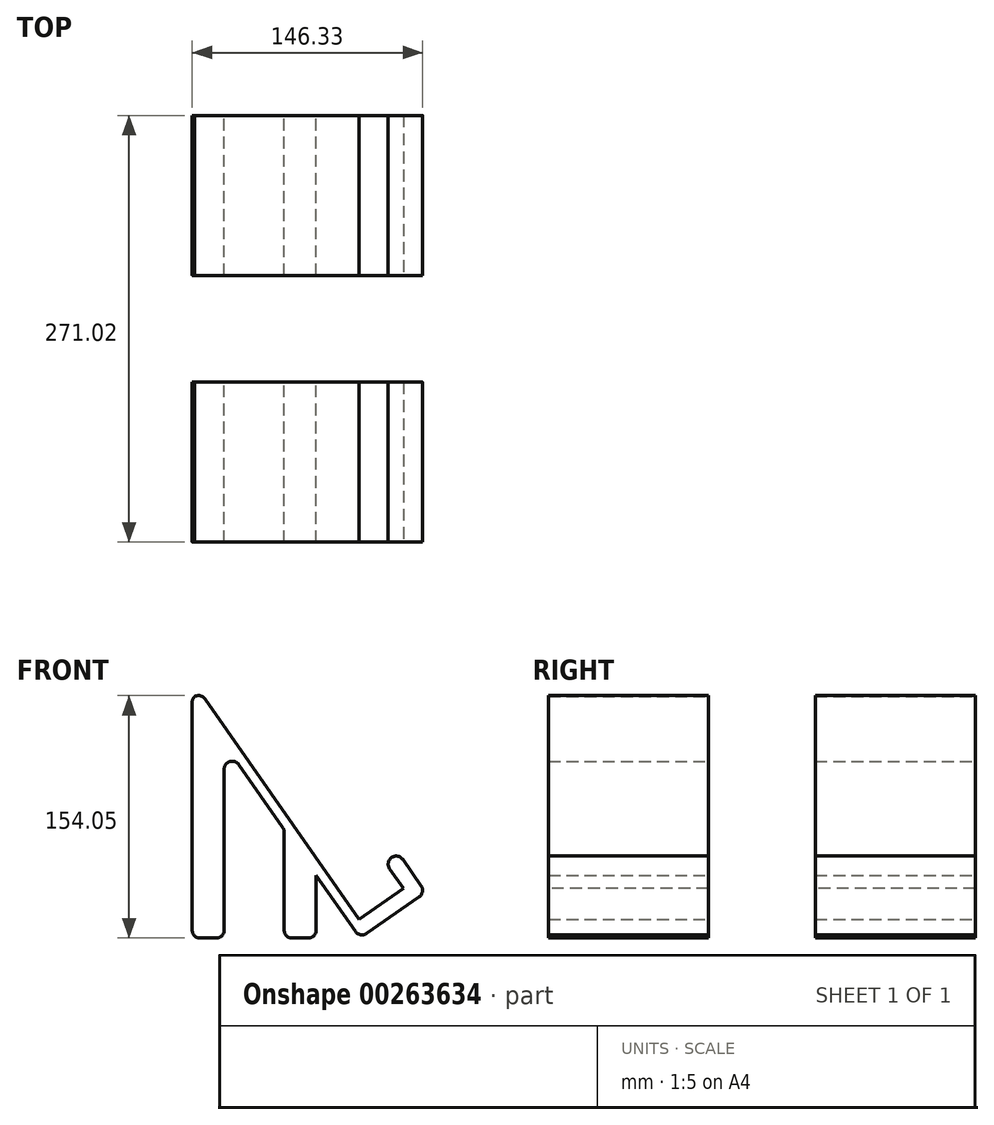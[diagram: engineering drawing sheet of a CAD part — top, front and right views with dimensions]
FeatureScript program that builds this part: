
annotation { "Feature Type Name" : "Feature", "Feature Type Description" : "" }
export const myFeature = defineFeature(function(context is Context, id is Id, definition is map)
    precondition{}
    {
        {
            var Q0;
            Q0=qCreatedBy(makeId("Front.planeOp"),FACE);
            var sketch = newSketch(context, id + "F0", { "sketchPlane" : qUnion([Q0])});
            skPoint(sketch, "E0.start.orphan", {"position": v(-59.33, -55.81) * mm});
            skPoint(sketch, "E1.start.orphan", {"position": v(-59.33, 20.12) * mm});
            skPoint(sketch, "E2.start.orphan", {"position": v(-103.17, -55.81) * mm});
            skLineSegment(sketch, "E3", {"start": v(-21.43, 93.97) * mm, "end": v(85.29, -58.43) * mm});
            skPoint(sketch, "E4.start.orphan", {"position": v(85.29, 87.57) * mm});
            skLineSegment(sketch, "E5", {"start": v(57.31, -58.43) * mm, "end": v(37, -58.43) * mm});
            skLineSegment(sketch, "E6.top", {"start": v(37, -58.43) * mm, "end": v(57.31, -58.43) * mm});
            skLineSegment(sketch, "E6.left", {"start": v(37, 10.54) * mm, "end": v(37, -58.43) * mm});
            skLineSegment(sketch, "E6.right", {"start": v(57.31, -18.48) * mm, "end": v(57.31, -58.43) * mm});
            skLineSegment(sketch, "E7.top", {"start": v(-21.43, -58.43) * mm, "end": v(-1.1, -58.43) * mm});
            skLineSegment(sketch, "E7.left", {"start": v(-21.43, 93.97) * mm, "end": v(-21.43, -58.43) * mm});
            skLineSegment(sketch, "E7.right", {"start": v(-1.1, 64.95) * mm, "end": v(-1.1, -58.43) * mm});
            skLineSegment(sketch, "E8.trimOffspring", {"start": v(-1.1, -58.43) * mm, "end": v(-21.43, -58.43) * mm});
            skLineSegment(sketch, "E9", {"start": v(-21.43, 93.97) * mm, "end": v(166, 93.97) * mm, "construction": true});
            skSolve(sketch);
        }
        {
            var Q0;
            Q0 = qSketchRegion(id + "F0", true);
            extrude(context, id + "F1", {"entities" : qUnion([Q0]), "depth" : 101.6 * mm});
        }
        {
            var Q0;
            {var subQ0=sQuery(id+"F0.wireOp",EDGE,"E3");Q0=makeQuery(id+"F1.opExtrude","SWEPT_FACE",FACE,{"disambiguationData":[OSD([subQ0]),TDD([makeQuery(id+"F0.imprint","IMPRINT",EDGE,{"disambiguationData":[TD([[makeQuery(id+"F0.imprint","INTERSECT",VERTEX,{"derivedFrom":[subQ0,sQuery(id+"F0.wireOp",EDGE,"E7.left")]}),-1.0]])],"derivedFrom":subQ0})])]});}
            var sketch = newSketch(context, id + "F2", { "sketchPlane" : qUnion([Q0])});
            skLineSegment(sketch, "E10.top", {"start": v(-101.6, -96.78) * mm, "end": v(0, -96.78) * mm});
            skLineSegment(sketch, "E10.left", {"start": v(-101.6, 89.27) * mm, "end": v(-101.6, -96.78) * mm});
            skLineSegment(sketch, "E10.right", {"start": v(0, 38.47) * mm, "end": v(0, -96.78) * mm});
            skLineSegment(sketch, "E11", {"start": v(-101.6, 89.27) * mm, "end": v(-101.6, 89.27) * mm});
            skLineSegment(sketch, "E12", {"start": v(0, 89.27) * mm, "end": v(-101.6, 89.27) * mm});
            skLineSegment(sketch, "E13", {"start": v(0, 38.47) * mm, "end": v(0, 89.27) * mm});
            skSolve(sketch);
        }
        {
            var Q0;
            Q0 = qSketchRegion(id + "F2", true);
            extrude(context, id + "F3", {"entities" : qUnion([Q0]), "operationType" : NewBodyOperationType.ADD, "depth" : 6.35 * mm});
        }
        {
            var Q0;
            Q0=makeQuery(id+"F3.opExtrude","CAP_FACE",FACE,{"disambiguationData":[OSD([sQuery(id+"F2.wireOp",EDGE,"E10.top"),sQuery(id+"F2.wireOp",EDGE,"E10.left"),sQuery(id+"F2.wireOp",EDGE,"E10.right"),sQuery(id+"F2.wireOp",EDGE,"E11"),sQuery(id+"F2.wireOp",EDGE,"E12"),sQuery(id+"F2.wireOp",EDGE,"E13")])],"isStart":false});
            var sketch = newSketch(context, id + "F4", { "sketchPlane" : qUnion([Q0])});
            skLineSegment(sketch, "E14.bottom", {"start": v(-101.6, -96.78) * mm, "end": v(0, -96.78) * mm});
            skLineSegment(sketch, "E14.top", {"start": v(-88.9, -86.62) * mm, "end": v(-12.7, -86.62) * mm});
            skLineSegment(sketch, "E14.left", {"start": v(-101.6, -96.78) * mm, "end": v(-101.6, -86.62) * mm});
            skLineSegment(sketch, "E14.right", {"start": v(0, -96.78) * mm, "end": v(0, -86.62) * mm});
            skLineSegment(sketch, "E15.top", {"start": v(-101.6, 20.8) * mm, "end": v(-88.9, 20.8) * mm});
            skLineSegment(sketch, "E15.left", {"start": v(-101.6, -86.62) * mm, "end": v(-101.6, 20.8) * mm});
            skLineSegment(sketch, "E15.right", {"start": v(-88.9, -86.62) * mm, "end": v(-88.9, 20.8) * mm});
            skLineSegment(sketch, "E16.top", {"start": v(0, 0.13) * mm, "end": v(-12.7, 0.13) * mm});
            skLineSegment(sketch, "E16.left", {"start": v(0, -86.62) * mm, "end": v(0, 0.13) * mm});
            skLineSegment(sketch, "E16.right", {"start": v(-12.7, -86.62) * mm, "end": v(-12.7, 0.13) * mm});
            skLineSegment(sketch, "E17", {"start": v(-88.9, -86.62) * mm, "end": v(-101.6, -86.62) * mm});
            skLineSegment(sketch, "E18", {"start": v(-12.7, -86.62) * mm, "end": v(0, -86.62) * mm});
            skSolve(sketch);
        }
        {
            var Q0;
            Q0=makeQuery(id+"F4.imprint","IMPRINT",FACE,{"disambiguationData":[TD([[makeQuery(id+"F4.imprint","IMPRINT",EDGE,{"derivedFrom":sQuery(id+"F4.wireOp",EDGE,"E14.bottom")}),1.0]])]});
            extrude(context, id + "F5", {"entities" : qUnion([Q0]), "operationType" : NewBodyOperationType.ADD, "depth" : 44.45 * mm});
        }
        {
            var Q0;
            Q0=makeQuery(id+"F5.opExtrude","SWEPT_FACE",FACE,{"disambiguationData":[OSD([sQuery(id+"F4.wireOp",EDGE,"E14.top"),sQuery(id+"F4.wireOp",EDGE,"E17"),sQuery(id+"F4.wireOp",EDGE,"E18")])]});
            var sketch = newSketch(context, id + "F6", { "sketchPlane" : qUnion([Q0])});
            skLineSegment(sketch, "E19.bottom", {"start": v(87.15, 0) * mm, "end": v(76.99, 0) * mm});
            skLineSegment(sketch, "E19.top", {"start": v(87.15, -101.6) * mm, "end": v(76.99, -101.6) * mm});
            skLineSegment(sketch, "E19.left", {"start": v(87.15, 0) * mm, "end": v(87.15, -101.6) * mm});
            skLineSegment(sketch, "E19.right", {"start": v(76.99, 0) * mm, "end": v(76.99, -101.6) * mm});
            skSolve(sketch);
        }
        {
            var Q0;
            Q0 = qSketchRegion(id + "F6", true);
            extrude(context, id + "F7", {"entities" : qUnion([Q0]), "operationType" : NewBodyOperationType.ADD, "depth" : 20.32 * mm});
        }
        {
            var Q0;
            Q0=makeQuery(id+"F7.opExtrude","CAP_EDGE",EDGE,{"disambiguationData":[OSD([sQuery(id+"F6.wireOp",EDGE,"E19.left")])],"isStart":false});
            var Q1;
            Q1=makeQuery(id+"F5.opExtrude","CAP_EDGE",EDGE,{"disambiguationData":[OSD([sQuery(id+"F4.wireOp",EDGE,"E14.bottom")])],"isStart":false});
            var Q2;
            Q2=makeQuery(id+"F7.opExtrude","CAP_EDGE",EDGE,{"disambiguationData":[OSD([sQuery(id+"F6.wireOp",EDGE,"E19.right")])],"isStart":false});
            var Q3;
            Q3=makeQuery(id+"F3.opExtrude","CAP_EDGE",EDGE,{"disambiguationData":[OSD([sQuery(id+"F2.wireOp",EDGE,"E12")])],"isStart":false});
            var Q4;
            Q4=makeQuery(id+"F3.opExtrude","CAP_EDGE",EDGE,{"disambiguationData":[OSD([sQuery(id+"F2.wireOp",EDGE,"E10.top")])],"isStart":true});
            var Q5;
            Q5=makeQuery(id+"F5.opExtrude","CAP_EDGE",EDGE,{"disambiguationData":[OSD([sQuery(id+"F4.wireOp",EDGE,"E14.top"),sQuery(id+"F4.wireOp",EDGE,"E17"),sQuery(id+"F4.wireOp",EDGE,"E18")])],"isStart":true});
            var Q6;
            Q6=makeQuery(id+"F3.boolean.opBoolean","MERGE",EDGE,{"derivedFrom":[makeQuery(id+"F1.opExtrude","SWEPT_EDGE",EDGE,{"disambiguationData":[OSD([sQuery(id+"F0.wireOp",EDGE,"E3"),sQuery(id+"F0.wireOp",EDGE,"E7.left")])]}),makeQuery(id+"F3.opExtrude","CAP_EDGE",EDGE,{"disambiguationData":[OSD([sQuery(id+"F2.wireOp",EDGE,"E12")])],"isStart":true})]});
            var Q7;
            Q7=makeQuery(id+"F1.opExtrude","SWEPT_EDGE",EDGE,{"disambiguationData":[OSD([sQuery(id+"F0.wireOp",EDGE,"E7.left"),sQuery(id+"F0.wireOp",EDGE,"E8.trimOffspring")])]});
            var Q8;
            Q8=makeQuery(id+"F1.opExtrude","SWEPT_EDGE",EDGE,{"disambiguationData":[OSD([sQuery(id+"F0.wireOp",EDGE,"E7.right"),sQuery(id+"F0.wireOp",EDGE,"E8.trimOffspring")])]});
            var Q9;
            Q9=makeQuery(id+"F1.opExtrude","SWEPT_EDGE",EDGE,{"disambiguationData":[OSD([sQuery(id+"F0.wireOp",EDGE,"E6.top"),sQuery(id+"F0.wireOp",EDGE,"E6.left")])]});
            var Q10;
            Q10=makeQuery(id+"F1.opExtrude","SWEPT_EDGE",EDGE,{"disambiguationData":[OSD([sQuery(id+"F0.wireOp",EDGE,"E6.top"),sQuery(id+"F0.wireOp",EDGE,"E6.right")])]});
            fillet(context, id + "F8", {"entities" : qUnion([Q0, Q1, Q2, Q3, Q4, Q5, Q6, Q7, Q8, Q9, Q10]), "radius" : 5.08 * mm, "tangentPropagation" : true, "allowEdgeOverflow" : false});
        }
        {
            var Q0;
            Q0=makeQuery(id+"F1.opExtrude","SWEPT_BODY",BODY,{"disambiguationData":[OSD([sQuery(id+"F0.wireOp",EDGE,"E3"),sQuery(id+"F0.wireOp",EDGE,"E7.left"),sQuery(id+"F0.wireOp",EDGE,"E7.right"),sQuery(id+"F0.wireOp",EDGE,"E8.trimOffspring")])]});
            transform(context, id + "F9", {"entities" : qUnion([Q0]), "transformType" : TransformType.TRANSLATION_3D, "dx" : 0 * mm, "dy" : 169.42 * mm, "dz" : 0 * mm, "makeCopy" : true});
        }
    });
